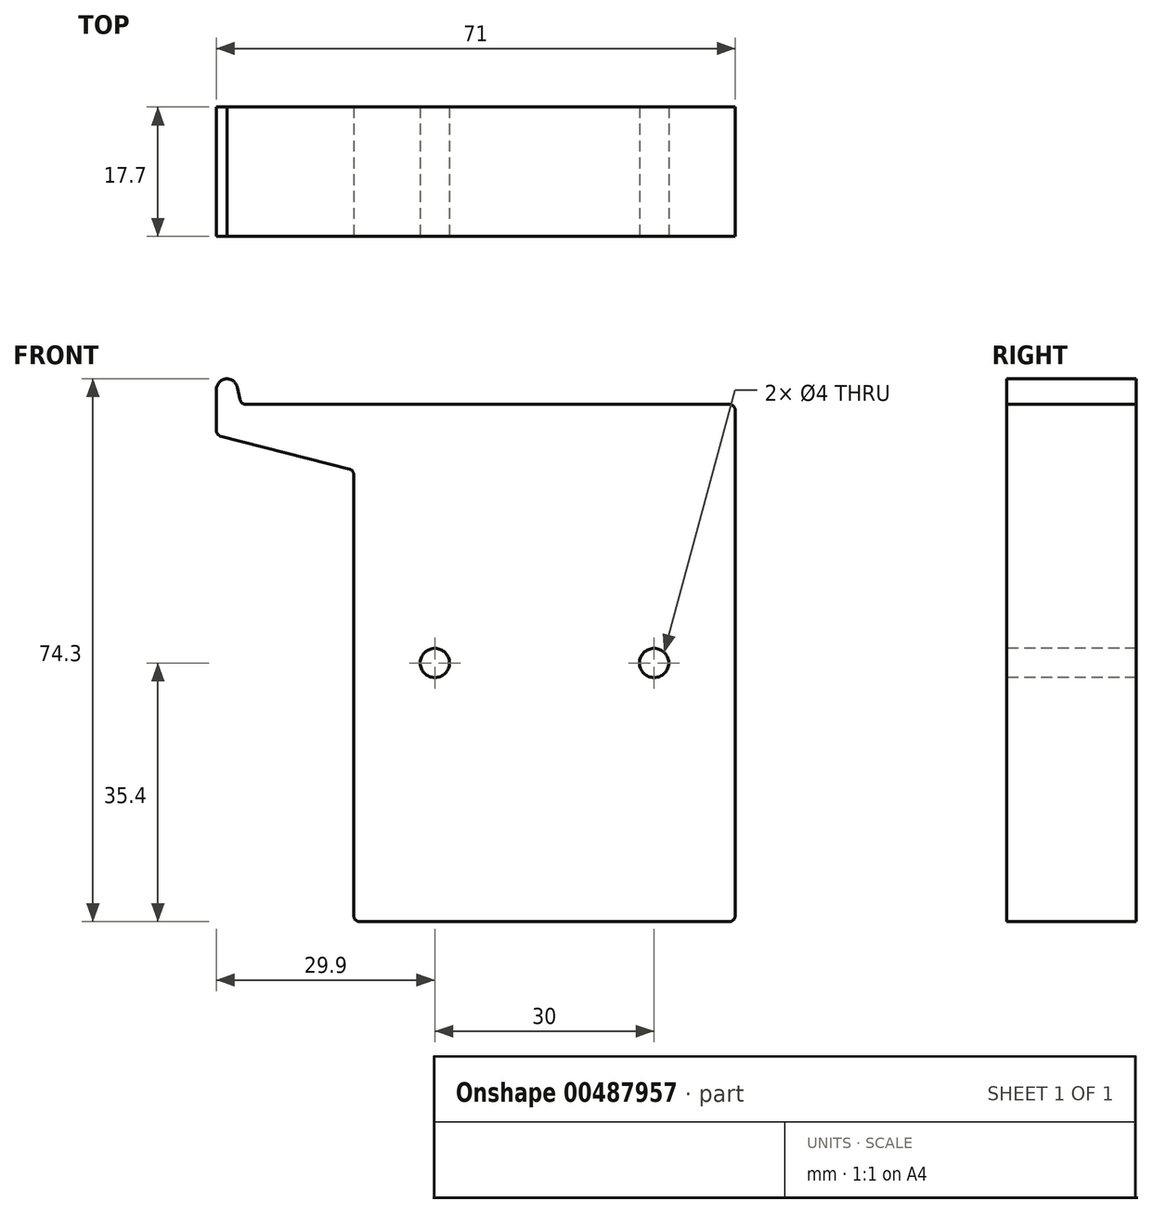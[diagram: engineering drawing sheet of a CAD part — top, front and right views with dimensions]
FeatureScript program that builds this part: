
annotation { "Feature Type Name" : "Feature", "Feature Type Description" : "" }
export const myFeature = defineFeature(function(context is Context, id is Id, definition is map)
    precondition{}
    {
        {
            var Q0;
            Q0=qCreatedBy(makeId("Front.planeOp"),FACE);
            var sketch = newSketch(context, id + "F0", { "sketchPlane" : qUnion([Q0])});
            skLineSegment(sketch, "E0.bottom", {"start": v(-41.5, 35.4) * mm, "end": v(26.1, 35.4) * mm});
            skLineSegment(sketch, "E0.top", {"start": v(-26.1, -35.4) * mm, "end": v(26.1, -35.4) * mm});
            skLineSegment(sketch, "E0.left", {"start": v(-26.1, 26.4) * mm, "end": v(-26.1, -35.4) * mm});
            skLineSegment(sketch, "E0.right", {"start": v(26.1, 35.4) * mm, "end": v(26.1, -35.4) * mm});
            skPoint(sketch, "E0.middle", {"position": v(0, 0) * mm});
            skCircle(sketch, "E1", {"center": v(-15, 0) * mm, "radius": 2 * mm});
            skCircle(sketch, "E2", {"center": v(15, 0) * mm, "radius": 2 * mm});
            skLineSegment(sketch, "E3", {"start": v(-41.5, 35.4) * mm, "end": v(-42.3, 38.9) * mm});
            skLineSegment(sketch, "E4", {"start": v(-42.3, 38.9) * mm, "end": v(-44.9, 38.9) * mm});
            skLineSegment(sketch, "E5", {"start": v(-44.9, 38.9) * mm, "end": v(-44.9, 31.2) * mm});
            skLineSegment(sketch, "E6", {"start": v(-44.9, 31.2) * mm, "end": v(-26.1, 26.4) * mm});
            skLineSegment(sketch, "E7", {"start": v(-26.1, 0) * mm, "end": v(26.1, 0) * mm, "construction": true});
            skLineSegment(sketch, "E8", {"start": v(0, 35.4) * mm, "end": v(0, -35.4) * mm, "construction": true});
            skLineSegment(sketch, "E9", {"start": v(-15, -2) * mm, "end": v(-15, 2) * mm, "construction": true});
            skSolve(sketch);
        }
        {
            var Q0;
            Q0=makeQuery(id+"F0.imprint","IMPRINT",FACE,{"disambiguationData":[TD([[makeQuery(id+"F0.imprint","IMPRINT",EDGE,{"derivedFrom":sQuery(id+"F0.wireOp",EDGE,"E0.bottom")}),-1.0]])]});
            extrude(context, id + "F1", {"entities" : qUnion([Q0]), "oppositeDirection" : true, "depth" : 17.7 * mm});
        }
        {
            var Q0;
            Q0=makeQuery(id+"F1.opExtrude","SWEPT_EDGE",EDGE,{"disambiguationData":[OSD([sQuery(id+"F0.wireOp",EDGE,"E4"),sQuery(id+"F0.wireOp",EDGE,"E5")])]});
            var Q1;
            Q1=makeQuery(id+"F1.opExtrude","SWEPT_EDGE",EDGE,{"disambiguationData":[OSD([sQuery(id+"F0.wireOp",EDGE,"E3"),sQuery(id+"F0.wireOp",EDGE,"E4")])]});
            fillet(context, id + "F2", {"entities" : qUnion([Q0, Q1]), "radius" : 1.5 * mm, "tangentPropagation" : true, "allowEdgeOverflow" : false});
        }
        {
            var Q0;
            Q0=makeQuery(id+"F1.opExtrude","SWEPT_EDGE",EDGE,{"disambiguationData":[OSD([sQuery(id+"F0.wireOp",EDGE,"E0.bottom"),sQuery(id+"F0.wireOp",EDGE,"E3")])]});
            var Q1;
            Q1=makeQuery(id+"F1.opExtrude","SWEPT_EDGE",EDGE,{"disambiguationData":[OSD([sQuery(id+"F0.wireOp",EDGE,"E0.bottom"),sQuery(id+"F0.wireOp",EDGE,"E0.right")])]});
            var Q2;
            Q2=makeQuery(id+"F1.opExtrude","SWEPT_EDGE",EDGE,{"disambiguationData":[OSD([sQuery(id+"F0.wireOp",EDGE,"E0.top"),sQuery(id+"F0.wireOp",EDGE,"E0.right")])]});
            var Q3;
            Q3=makeQuery(id+"F1.opExtrude","SWEPT_EDGE",EDGE,{"disambiguationData":[OSD([sQuery(id+"F0.wireOp",EDGE,"E5"),sQuery(id+"F0.wireOp",EDGE,"E6")])]});
            var Q4;
            Q4=makeQuery(id+"F1.opExtrude","SWEPT_EDGE",EDGE,{"disambiguationData":[OSD([sQuery(id+"F0.wireOp",EDGE,"E0.left"),sQuery(id+"F0.wireOp",EDGE,"E6")])]});
            var Q5;
            Q5=makeQuery(id+"F1.opExtrude","SWEPT_EDGE",EDGE,{"disambiguationData":[OSD([sQuery(id+"F0.wireOp",EDGE,"E0.top"),sQuery(id+"F0.wireOp",EDGE,"E0.left")])]});
            fillet(context, id + "F3", {"entities" : qUnion([Q0, Q1, Q2, Q3, Q4, Q5]), "radius" : 0.8 * mm, "tangentPropagation" : true, "allowEdgeOverflow" : false});
        }
    });
